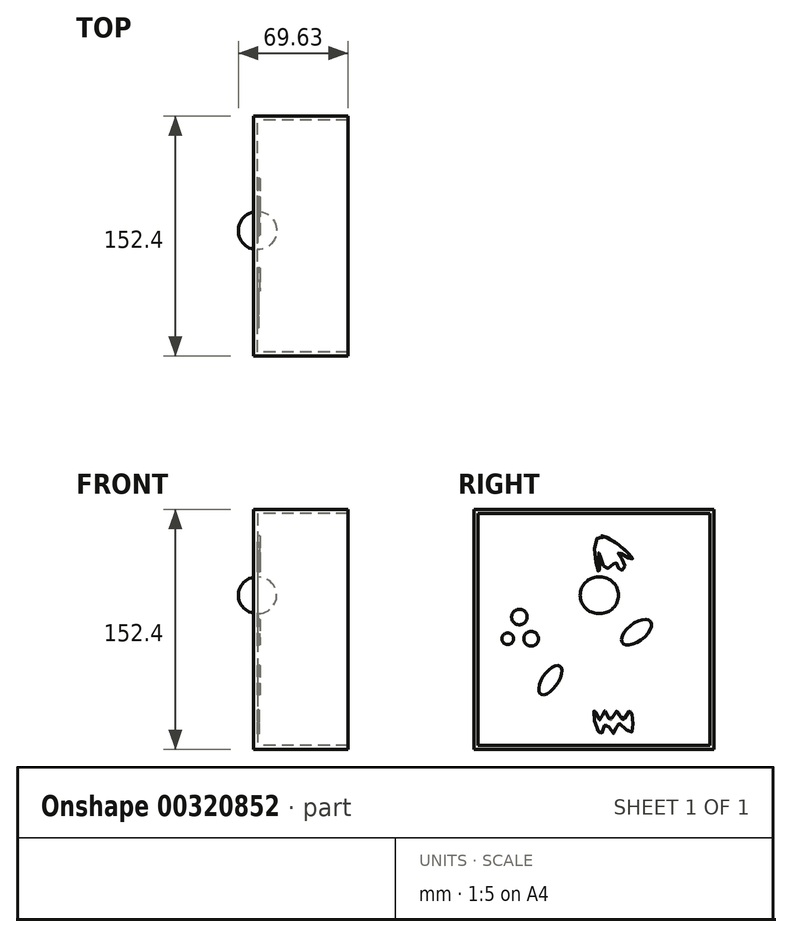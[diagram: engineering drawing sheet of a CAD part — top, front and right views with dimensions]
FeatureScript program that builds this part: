
annotation { "Feature Type Name" : "Feature", "Feature Type Description" : "" }
export const myFeature = defineFeature(function(context is Context, id is Id, definition is map)
    precondition{}
    {
        {
            var Q0;
            Q0=qCreatedBy(makeId("Right.planeOp"),FACE);
            var sketch = newSketch(context, id + "F0", { "sketchPlane" : qUnion([Q0])});
            skLineSegment(sketch, "E0.bottom", {"start": v(0, 0) * mm, "end": v(152.4, 0) * mm});
            skLineSegment(sketch, "E0.top", {"start": v(0, -152.4) * mm, "end": v(152.4, -152.4) * mm});
            skLineSegment(sketch, "E0.left", {"start": v(0, 0) * mm, "end": v(0, -152.4) * mm});
            skLineSegment(sketch, "E0.right", {"start": v(152.4, 0) * mm, "end": v(152.4, -152.4) * mm});
            skSolve(sketch);
        }
        {
            var Q0;
            Q0=makeQuery(id+"F0.imprint","IMPRINT",FACE,{"disambiguationData":[TD([[makeQuery(id+"F0.imprint","IMPRINT",EDGE,{"derivedFrom":sQuery(id+"F0.wireOp",EDGE,"E0.bottom")}),-1.0]])]});
            extrude(context, id + "F1", {"entities" : qUnion([Q0]), "depth" : 60 * mm});
        }
        {
            var Q0;
            Q0=makeQuery(id+"F1.opExtrude","CAP_FACE",FACE,{"disambiguationData":[OSD([sQuery(id+"F0.wireOp",EDGE,"E0.bottom"),sQuery(id+"F0.wireOp",EDGE,"E0.top"),sQuery(id+"F0.wireOp",EDGE,"E0.left"),sQuery(id+"F0.wireOp",EDGE,"E0.right")])],"isStart":false});
            shell(context, id + "F2", {"entities" : qUnion([Q0]), "thickness" : 2.54 * mm});
        }
        {
            var Q0;
            Q0=makeQuery(id+"F2.opShell","OFFSET_FACE",FACE,{"disambiguationData":[OSD([sQuery(id+"F0.wireOp",EDGE,"E0.bottom"),sQuery(id+"F0.wireOp",EDGE,"E0.top"),sQuery(id+"F0.wireOp",EDGE,"E0.left"),sQuery(id+"F0.wireOp",EDGE,"E0.right")])]});
            var sketch = newSketch(context, id + "F3", { "sketchPlane" : qUnion([Q0])});
            skLineSegment(sketch, "E1", {"start": v(79.66, -42.94) * mm, "end": v(79.66, -65.97) * mm});
            skArc(sketch, "E2", {"start": v(79.66, -65.97) * mm, "mid": v(91.83, -54.45) * mm, "end": v(79.66, -42.94) * mm});
            skSolve(sketch);
        }
        {
            var Q0;
            Q0 = qSketchRegion(id + "F3", true);
            var Q1;
            Q1=sQuery(id+"F3.wireOp",EDGE,"E1");
            revolve(context, id + "F4", {"operationType" : NewBodyOperationType.ADD, "entities" : qUnion([Q0]), "axis" : qUnion([Q1]), "revolveType" : RevolveType.FULL});
        }
        {
            var Q0;
            Q0=makeQuery(id+"F3.imprint","IMPRINT",FACE,{"disambiguationData":[TD([[makeQuery(id+"F3.imprint","IMPRINT",EDGE,{"derivedFrom":sQuery(id+"F3.wireOp",EDGE,"E1")}),-1.0]])]});
            var sketch = newSketch(context, id + "F5", { "sketchPlane" : qUnion([Q0])});
            skEllipse(sketch, "E3", {"center": v(48.52, -108.4) * mm, "majorRadius": 10.78 * mm, "minorRadius": 5 * mm, "majorAxis": v(0.57, 0.82)});
            skEllipse(sketch, "E4", {"center": v(103.31, -77.92) * mm, "majorRadius": 11.21 * mm, "minorRadius": 5.63 * mm, "majorAxis": v(0.8, 0.61)});
            skSolve(sketch);
        }
        {
            var Q0;
            Q0 = qSketchRegion(id + "F5", true);
            extrude(context, id + "F6", {"entities" : qUnion([Q0]), "depth" : 1.5 * mm});
        }
        {
            var Q0;
            Q0=makeQuery(id+"F3.imprint","IMPRINT",FACE,{"disambiguationData":[TD([[makeQuery(id+"F3.imprint","IMPRINT",EDGE,{"derivedFrom":sQuery(id+"F3.wireOp",EDGE,"E1")}),-1.0]])]});
            var sketch = newSketch(context, id + "F7", { "sketchPlane" : qUnion([Q0])});
            skCircle(sketch, "E5", {"center": v(21.48, -82.1) * mm, "radius": 3.68 * mm});
            skCircle(sketch, "E6", {"center": v(28.86, -68.32) * mm, "radius": 4.91 * mm});
            skCircle(sketch, "E7", {"center": v(36.31, -82.1) * mm, "radius": 4.66 * mm});
            skSolve(sketch);
        }
        {
            var Q0;
            Q0 = qSketchRegion(id + "F7", true);
            extrude(context, id + "F8", {"entities" : qUnion([Q0]), "depth" : 0.5 * mm});
        }
        {
            var Q0;
            Q0=makeQuery(id+"F3.imprint","IMPRINT",FACE,{"disambiguationData":[TD([[makeQuery(id+"F3.imprint","IMPRINT",EDGE,{"derivedFrom":sQuery(id+"F3.wireOp",EDGE,"E1")}),-1.0]])]});
            var sketch = newSketch(context, id + "F9", { "sketchPlane" : qUnion([Q0])});
            skFitSpline(sketch, "E8", {"points": [v(95.94, -36) * mm, v(92.4, -38.31) * mm, v(90.1, -33.55) * mm, v(83.88, -37.54) * mm, v(79.34, -27.48) * mm, v(79.44, -39.7) * mm, v(79.17, -17.3) * mm, v(100.77, -31.54) * mm, v(91.6, -27.26) * mm, v(95.94, -36) * mm]});
            skSolve(sketch);
        }
        {
            var Q0;
            Q0 = qSketchRegion(id + "F9", true);
            extrude(context, id + "F10", {"entities" : qUnion([Q0]), "depth" : 1.5 * mm});
        }
        {
            var Q0;
            Q0=makeQuery(id+"F3.imprint","IMPRINT",FACE,{"disambiguationData":[TD([[makeQuery(id+"F3.imprint","IMPRINT",EDGE,{"derivedFrom":sQuery(id+"F3.wireOp",EDGE,"E1")}),-1.0]])]});
            var sketch = newSketch(context, id + "F11", { "sketchPlane" : qUnion([Q0])});
            skFitSpline(sketch, "E9", {"points": [v(76.6, -134.3) * mm, v(76.82, -127.47) * mm, v(80.32, -133.88) * mm, v(82.76, -127.64) * mm, v(86.81, -133.8) * mm, v(90.4, -128.18) * mm, v(94.68, -133.26) * mm, v(98.84, -127.8) * mm, v(100.87, -134.16) * mm, v(99.28, -141.84) * mm, v(91.58, -135.86) * mm, v(88.98, -142.34) * mm, v(83.87, -136.3) * mm, v(81.1, -142.3) * mm, v(76.6, -134.3) * mm]});
            skSolve(sketch);
        }
        {
            var Q0;
            Q0 = qSketchRegion(id + "F11", true);
            extrude(context, id + "F12", {"entities" : qUnion([Q0]), "depth" : 1 * mm});
        }
    });
